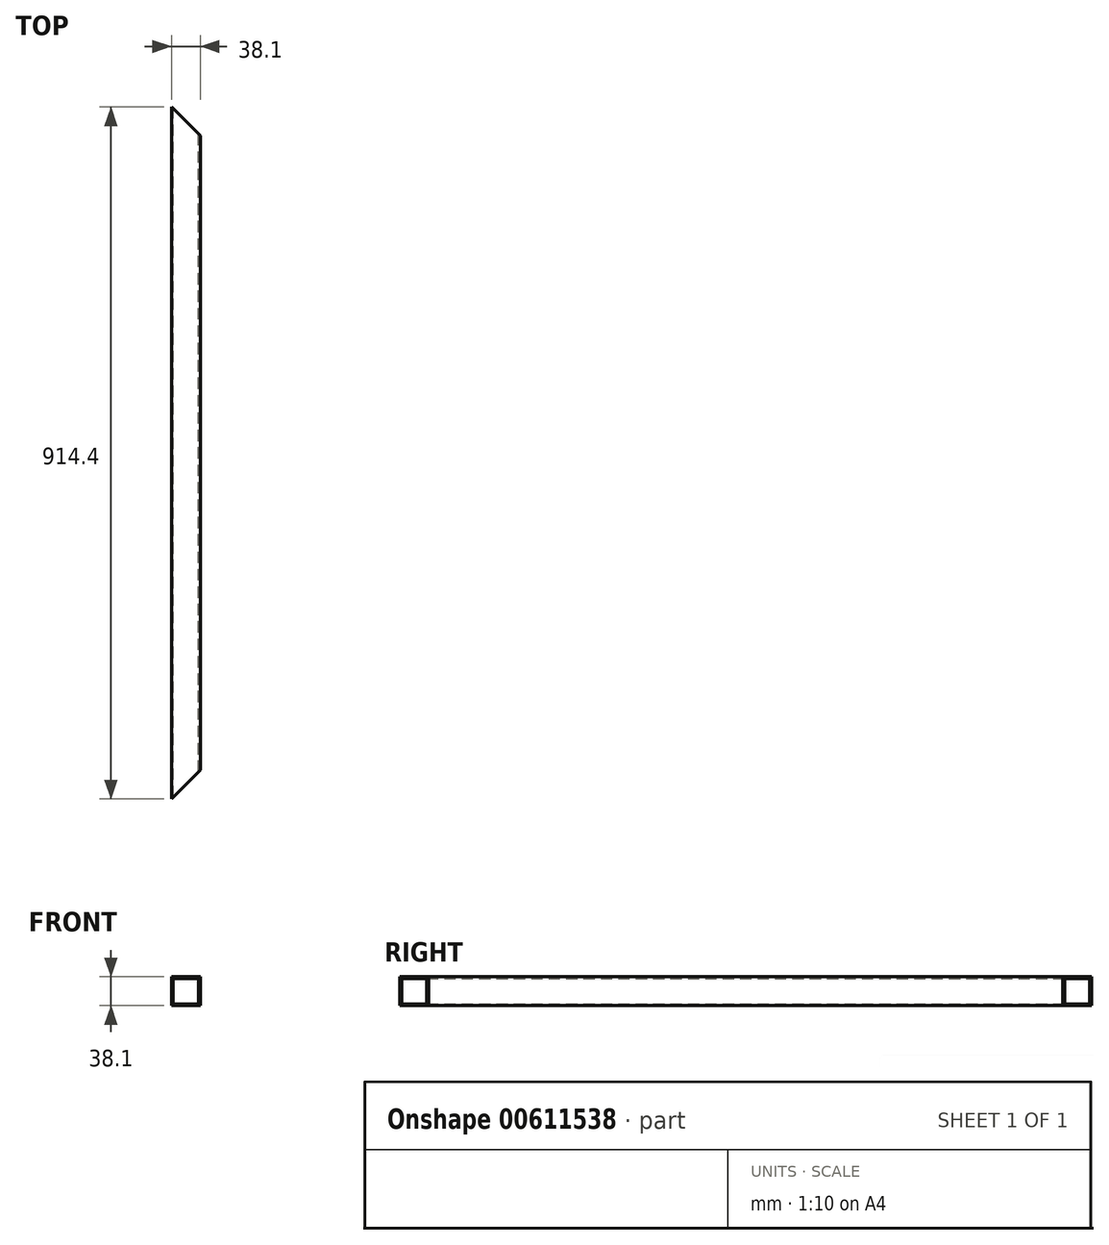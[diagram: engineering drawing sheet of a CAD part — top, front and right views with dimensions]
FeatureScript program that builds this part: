
annotation { "Feature Type Name" : "Feature", "Feature Type Description" : "" }
export const myFeature = defineFeature(function(context is Context, id is Id, definition is map)
    precondition{}
    {
        {
            var Q0;
            Q0=qCreatedBy(makeId("Front.planeOp"),FACE);
            var sketch = newSketch(context, id + "F0", { "sketchPlane" : qUnion([Q0])});
            skLineSegment(sketch, "E0.bottom", {"start": v(0, 0) * mm, "end": v(-38.1, 0) * mm});
            skLineSegment(sketch, "E0.top", {"start": v(0, -38.1) * mm, "end": v(-38.1, -38.1) * mm});
            skLineSegment(sketch, "E0.left", {"start": v(0, 0) * mm, "end": v(0, -38.1) * mm});
            skLineSegment(sketch, "E0.right", {"start": v(-38.1, 0) * mm, "end": v(-38.1, -38.1) * mm});
            skLineSegment(sketch, "E1.bottom", {"start": v(-35.81, -2.29) * mm, "end": v(-2.29, -2.29) * mm});
            skLineSegment(sketch, "E1.top", {"start": v(-35.81, -35.81) * mm, "end": v(-2.29, -35.81) * mm});
            skLineSegment(sketch, "E1.left", {"start": v(-35.81, -2.29) * mm, "end": v(-35.81, -35.81) * mm});
            skLineSegment(sketch, "E1.right", {"start": v(-2.29, -2.29) * mm, "end": v(-2.29, -35.81) * mm});
            skSolve(sketch);
        }
        {
            var Q0;
            Q0 = qSketchRegion(id + "F0", true);
            extrude(context, id + "F1", {"entities" : qUnion([Q0]), "depth" : 914.4 * mm, "offsetDistance" : 25.4 * mm});
        }
        {
            var Q0;
            Q0=makeQuery(id+"F1.opExtrude","SWEPT_FACE",FACE,{"disambiguationData":[OSD([sQuery(id+"F0.wireOp",EDGE,"E0.bottom")])]});
            var sketch = newSketch(context, id + "F2", { "sketchPlane" : qUnion([Q0])});
            skLineSegment(sketch, "E2", {"start": v(-38.1, -914.4) * mm, "end": v(0, -876.3) * mm});
            skLineSegment(sketch, "E3", {"start": v(0, -876.3) * mm, "end": v(0, -914.4) * mm});
            skLineSegment(sketch, "E4", {"start": v(0, -914.4) * mm, "end": v(-38.1, -914.4) * mm});
            skLineSegment(sketch, "E5", {"start": v(-38.1, 0) * mm, "end": v(0, -38.1) * mm});
            skLineSegment(sketch, "E6", {"start": v(0, -38.1) * mm, "end": v(0, 0) * mm});
            skLineSegment(sketch, "E7", {"start": v(0, 0) * mm, "end": v(-38.1, 0) * mm});
            skSolve(sketch);
        }
        {
            var Q0;
            Q0 = qSketchRegion(id + "F2", true);
            extrude(context, id + "F3", {"entities" : qUnion([Q0]), "operationType" : NewBodyOperationType.REMOVE, "oppositeDirection" : true, "depth" : 50.8 * mm, "offsetDistance" : 25.4 * mm});
        }
    });
